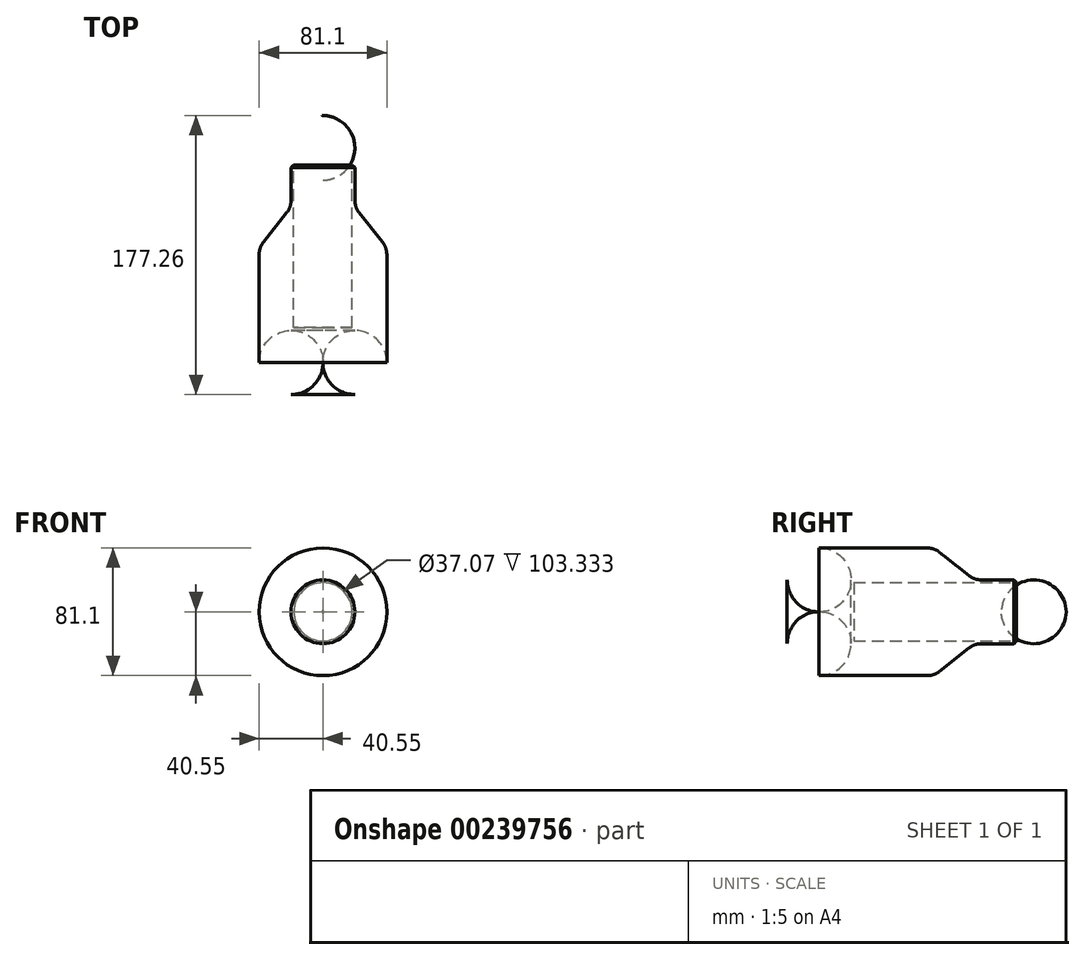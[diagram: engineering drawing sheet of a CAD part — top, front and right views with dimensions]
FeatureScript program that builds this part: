
annotation { "Feature Type Name" : "Feature", "Feature Type Description" : "" }
export const myFeature = defineFeature(function(context is Context, id is Id, definition is map)
    precondition{}
    {
        {
            var Q0;
            Q0=qCreatedBy(makeId("Top.planeOp"),FACE);
            var sketch = newSketch(context, id + "F0", { "sketchPlane" : qUnion([Q0])});
            skLineSegment(sketch, "E0", {"start": v(0, 84.04) * mm, "end": v(0, 84.03) * mm});
            skLineSegment(sketch, "E1", {"start": v(0, -93.22) * mm, "end": v(20.23, -93.22) * mm});
            skLineSegment(sketch, "E2", {"start": v(40.55, -72.9) * mm, "end": v(40.55, -4.27) * mm});
            skLineSegment(sketch, "E3", {"start": v(37.79, 3.63) * mm, "end": v(23.03, 22.2) * mm});
            skLineSegment(sketch, "E4", {"start": v(20.27, 30.1) * mm, "end": v(20.27, 63.46) * mm});
            skLineSegment(sketch, "E5", {"start": v(0, 84.04) * mm, "end": v(-0.61, 84.03) * mm});
            skPoint(sketch, "E6.visualSharp", {"position": v(20.27, 25.67) * mm});
            skArc(sketch, "E6.filletArc", {"start": v(20.27, 30.1) * mm, "mid": v(20.98, 25.92) * mm, "end": v(23.03, 22.2) * mm});
            skPoint(sketch, "E7.visualSharp", {"position": v(40.55, 0.16) * mm});
            skArc(sketch, "E7.filletArc", {"start": v(40.55, -4.27) * mm, "mid": v(39.84, -0.08) * mm, "end": v(37.79, 3.63) * mm});
            skPoint(sketch, "E8.visualSharp", {"position": v(20.27, 84.35) * mm});
            skArc(sketch, "E8.filletArc", {"start": v(0, 84.03) * mm, "mid": v(-0.3, 84.03) * mm, "end": v(-0.61, 84.03) * mm});
            skPoint(sketch, "E9.visualSharp", {"position": v(40.55, -93.22) * mm});
            skArc(sketch, "E9.filletArc", {"start": v(20.23, -93.22) * mm, "mid": v(34.6, -87.27) * mm, "end": v(40.55, -72.9) * mm});
            skLineSegment(sketch, "E10", {"start": v(-0.3, 63.46) * mm, "end": v(20.27, 63.46) * mm});
            skLineSegment(sketch, "E11.trimOffspring", {"start": v(0, 63.46) * mm, "end": v(0, -93.22) * mm});
            skSolve(sketch);
        }
        {
            var Q0;
            Q0 = qSketchRegion(id + "F0", true);
            var Q1;
            Q1=sQuery(id+"F0.wireOp",EDGE,"E0");
            revolve(context, id + "F1", {"entities" : qUnion([Q0]), "axis" : qUnion([Q1]), "revolveType" : RevolveType.FULL});
        }
        {
            var Q0;
            Q0=qCreatedBy(makeId("Top.planeOp"),FACE);
            var sketch = newSketch(context, id + "F2", { "sketchPlane" : qUnion([Q0])});
            skLineSegment(sketch, "E12", {"start": v(0, 21.35) * mm, "end": v(23.98, 21.35) * mm});
            skLineSegment(sketch, "E13", {"start": v(23.98, 21.35) * mm, "end": v(8.4, 62.88) * mm});
            skLineSegment(sketch, "E14", {"start": v(8.4, 62.88) * mm, "end": v(0, 62.88) * mm});
            skLineSegment(sketch, "E15", {"start": v(0, 62.88) * mm, "end": v(0, 21.35) * mm});
            skSolve(sketch);
        }
        {
            var Q0;
            Q0 = qSketchRegion(id + "F2", true);
            var Q1;
            Q1=sQuery(id+"F2.wireOp",EDGE,"E15");
            revolve(context, id + "F3", {"entities" : qUnion([Q0]), "axis" : qUnion([Q1]), "revolveType" : RevolveType.FULL});
        }
        {
            var Q0;
            Q0=makeQuery(id+"F3.opRevolve","SWEPT_BODY",BODY,{"disambiguationData":[OSD([sQuery(id+"F2.wireOp",EDGE,"E12"),sQuery(id+"F2.wireOp",EDGE,"E13"),sQuery(id+"F2.wireOp",EDGE,"E14"),sQuery(id+"F2.wireOp",EDGE,"E15")])]});
            deleteBodies(context, id + "F4", {"entities" : qUnion([Q0])});
        }
        {
            var Q0;
            Q0=makeQuery(id+"F1.opRevolve","SWEPT_FACE",FACE,{"disambiguationData":[OSD([sQuery(id+"F0.wireOp",EDGE,"E10")])]});
            var sketch = newSketch(context, id + "F5", { "sketchPlane" : qUnion([Q0])});
            skCircle(sketch, "E16", {"center": v(0, 0) * mm, "radius": 18.54 * mm});
            skSolve(sketch);
        }
        {
            var Q0;
            Q0 = qSketchRegion(id + "F5", true);
            extrude(context, id + "F6", {"entities" : qUnion([Q0]), "operationType" : NewBodyOperationType.REMOVE, "oppositeDirection" : true, "depth" : 114.3 * mm});
        }
        {
            var Q0;
            Q0=makeQuery(id+"F1.opRevolve","SWEPT_EDGE",EDGE,{"disambiguationData":[OSD([sQuery(id+"F0.wireOp",EDGE,"E4"),sQuery(id+"F0.wireOp",EDGE,"E10")])]});
            chamfer(context, id + "F7", {"entities" : qUnion([Q0]), "width" : 12.7 * mm, "tangentPropagation" : true});
        }
    });
